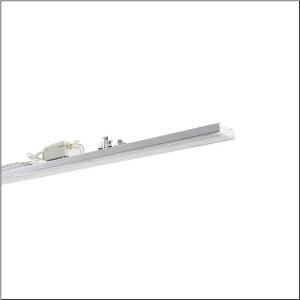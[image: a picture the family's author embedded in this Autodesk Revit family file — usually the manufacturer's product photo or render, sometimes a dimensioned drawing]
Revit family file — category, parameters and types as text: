
# Revit family: licross_r__21_recessed_mo_52tl19dv4e5g_1e2e
name_source: partatom
category: Lighting Fixtures
units: mm (PartAtom-declared; Revit-internal decimal feet)

## family parameters
Cut with Voids When Loaded = No
Host = Face
Light Source = No
Part Type = Normal
Room Calculation Point = No
Round Connector Dimension = Use Diameter
Shared = No

## types (1)
- --- (1 x LED, 14780 lm, 85.3 W, 4000K)
    Apparent Load = 85 VA
    CIE Flux Codes = 55 90 98 100 100
    Color Rendering = 80
    Color Temperature = 4000K
    Default Elevation = 1800 mm
    Description = Licross® 21 Recessed MO, luminaire insert, of sheet steel, galvanised, coil coated, white, length: 2.250mm, width: 66mm, height: 67mm, LED rated luminous flux: 14.780lm, light colour: 840, control gear: DALI 2, with plug, 5-pole, with phase selection, mains connection: 220..240V, AC, 50/60Hz, rated input power: 85W, halogen-free wiring, primary light control with lens, of plastic, primary optical cover: cover, of PMMA, light emission: direct distribution, primary light characteristic: double asymmetric, protection rating (complete): IP40, insulation class (complete): insulation class I (protective earthing), certification: CE, ENEC, VDE, UKCA, protection symbol: D if used in an environment without relevant dust loads with corresponding accessories, impact resistance: IK06, permissible ambient temperature for indoor applications: -25..+35°C, corresponds to IFS (International Featured Standards) requirements for safety and quality in the food industry, reducing of maximum allowable ambient temperature of 5°C with ceiling mounting, LABS conformity tested according to VDMA 24364:2018-05, packaging unit: 1 piece
    Height = 58 mm
    Lamp = 1 x LED
    Lamp Light Flux = 14780 lm
    Lamp Power = 85.3 W
    Lamp count = 1
    Length = 2250 mm
    Luminous efficacy = 173 lm/W
    Manufacturer = Siteco
    ModVariant = No
    Model = 52TL19DV4E5G
    Mounting Place = Ceiling
    Mounting Type = Pendant
    Number of Poles = 1
    OnlyDefault = Yes
    Power Factor = 1
    Product Name = Licross® 21 Recessed MO
    Product group = luminaire insert
    ProductGroupID = 901
    Protection Class = Protection class I
    Protection Degree = IP 40
    RLX_Detail_Level = 1
    RLX_Emergency_Light_Flux = 0 lm
    RLX_Emergency_Type = 0
    RLX_Emergency_Type_DB = No
    RlxData = <blob elided: 29693 chars, md5=50b12853>
    Socket = socket
    Standby Power = 0 W
    System Light Flux = 14780 lm
    System Power = 85 W
    Type Comments = factory setting: luminous flux: 100 % | dim-lin: 254 | 390 mA
    Type Image = l_1296930.jpg
    URL = http://relux.com
    VarID = @adj_059661
    Voltage = 0 V
    Weight = 0.00 kg
    Width = 66 mm

## geometry (parser evidence)
native form markers: Blend x4, Sweep x9
no freeform markers — native parametric forms only
